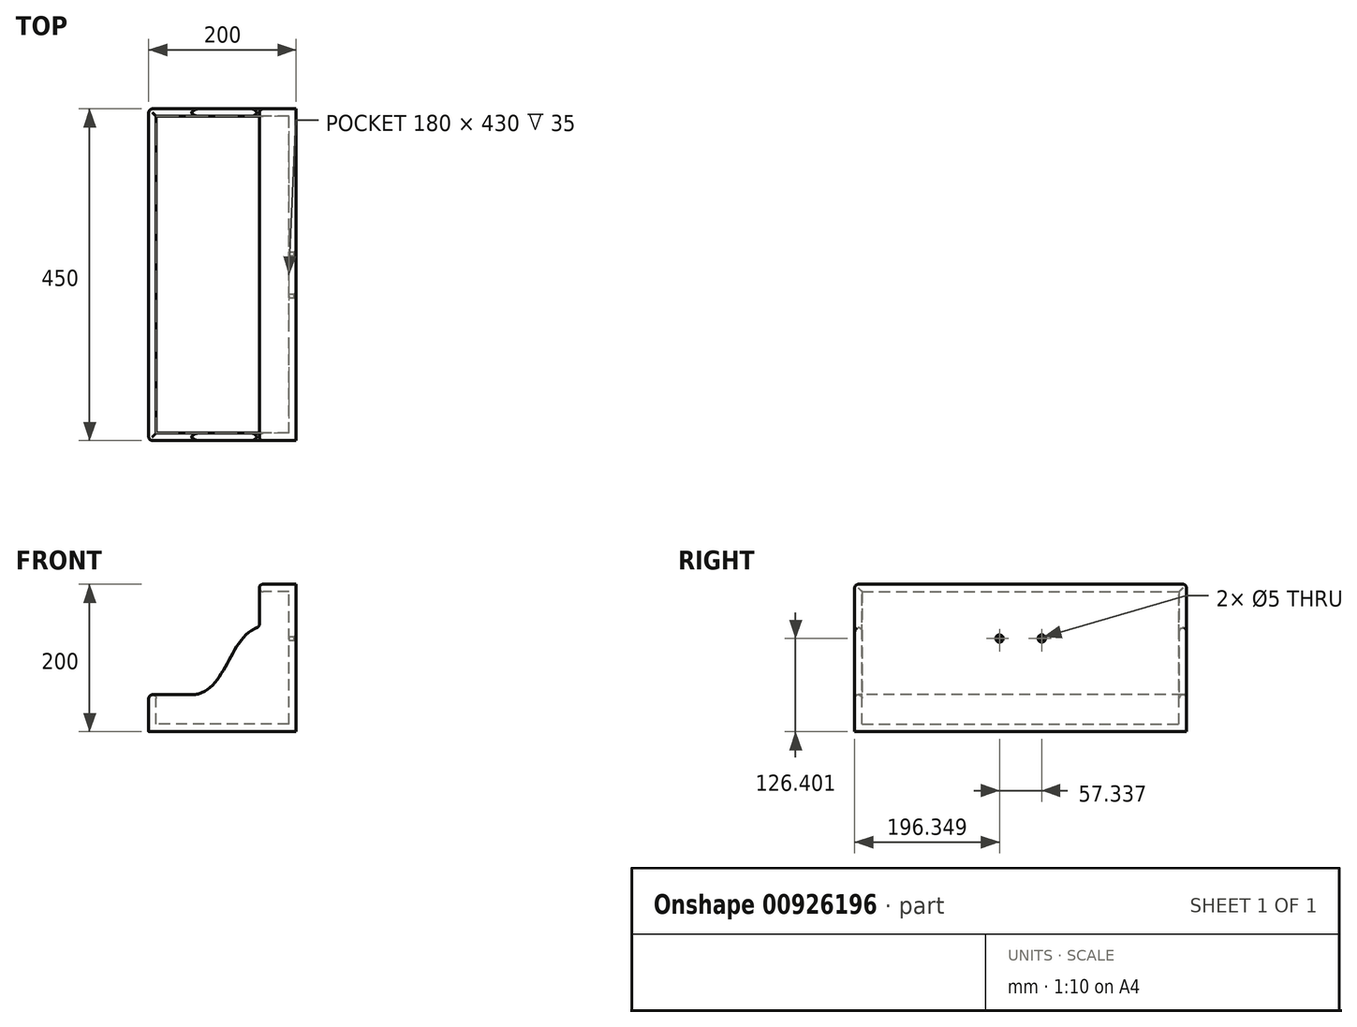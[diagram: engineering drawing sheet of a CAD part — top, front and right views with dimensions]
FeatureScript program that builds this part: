
annotation { "Feature Type Name" : "Feature", "Feature Type Description" : "" }
export const myFeature = defineFeature(function(context is Context, id is Id, definition is map)
    precondition{}
    {
        {
            var Q0;
            Q0=qCreatedBy(makeId("Front.planeOp"),FACE);
            var sketch = newSketch(context, id + "F0", { "sketchPlane" : qUnion([Q0])});
            skLineSegment(sketch, "E0", {"start": v(0, 0) * mm, "end": v(-200, 0) * mm});
            skLineSegment(sketch, "E1", {"start": v(-200, 0) * mm, "end": v(-200, 50) * mm});
            skLineSegment(sketch, "E2", {"start": v(-200, 50) * mm, "end": v(-142.3, 50) * mm});
            skLineSegment(sketch, "E3", {"start": v(0, 0) * mm, "end": v(0, 200) * mm});
            skLineSegment(sketch, "E4", {"start": v(0, 200) * mm, "end": v(-50, 200) * mm});
            skLineSegment(sketch, "E5", {"start": v(-50, 200) * mm, "end": v(-50, 142.3) * mm});
            skFitSpline(sketch, "E6", {"points": [v(-142.3, 50) * mm, v(-50, 142.3) * mm], "startDerivative": vector(145.52, 2.79) * mm, "endDerivative": vector(131.39, 42.95) * mm});
            skSolve(sketch);
        }
        {
            var Q0;
            Q0=makeQuery(id+"F0.imprint","IMPRINT",FACE,{"disambiguationData":[TD([[makeQuery(id+"F0.imprint","IMPRINT",EDGE,{"derivedFrom":sQuery(id+"F0.wireOp",EDGE,"E0")}),-1.0]])]});
            extrude(context, id + "F1", {"entities" : qUnion([Q0]), "depth" : 450 * mm, "offsetDistance" : 25 * mm});
        }
        {
            var Q0;
            Q0=makeQuery(id+"F1.opExtrude","SWEPT_FACE",FACE,{"disambiguationData":[OSD([sQuery(id+"F0.wireOp",EDGE,"E6")])]});
            var Q1;
            Q1=makeQuery(id+"F1.opExtrude","SWEPT_FACE",FACE,{"disambiguationData":[OSD([sQuery(id+"F0.wireOp",EDGE,"E5")])]});
            var Q2;
            Q2=makeQuery(id+"F1.opExtrude","SWEPT_FACE",FACE,{"disambiguationData":[OSD([sQuery(id+"F0.wireOp",EDGE,"E2")])]});
            shell(context, id + "F2", {"entities" : qUnion([Q0, Q1, Q2]), "thickness" : 10 * mm});
        }
        {
            var Q0;
            Q0=makeQuery(id+"F1.opExtrude","SWEPT_FACE",FACE,{"disambiguationData":[OSD([sQuery(id+"F0.wireOp",EDGE,"E5")])]});
            var Q1;
            Q1=makeQuery(id+"F1.opExtrude","SWEPT_FACE",FACE,{"disambiguationData":[OSD([sQuery(id+"F0.wireOp",EDGE,"E2")])]});
            var Q2;
            Q2=makeQuery(id+"F1.opExtrude","CAP_EDGE",EDGE,{"disambiguationData":[OSD([sQuery(id+"F0.wireOp",EDGE,"E1")])],"isStart":false});
            var Q3;
            Q3=makeQuery(id+"F1.opExtrude","CAP_EDGE",EDGE,{"disambiguationData":[OSD([sQuery(id+"F0.wireOp",EDGE,"E1")])],"isStart":true});
            var Q4;
            Q4=makeQuery(id+"F1.opExtrude","CAP_EDGE",EDGE,{"disambiguationData":[OSD([sQuery(id+"F0.wireOp",EDGE,"E4")])],"isStart":false});
            var Q5;
            Q5=makeQuery(id+"F1.opExtrude","CAP_EDGE",EDGE,{"disambiguationData":[OSD([sQuery(id+"F0.wireOp",EDGE,"E4")])],"isStart":true});
            fillet(context, id + "F3", {"entities" : qUnion([Q0, Q1, Q2, Q3, Q4, Q5]), "radius" : 5 * mm, "tangentPropagation" : true, "allowEdgeOverflow" : false});
        }
        {
            var Q0;
            Q0=qCreatedBy(makeId("Right.planeOp"),FACE);
            var sketch = newSketch(context, id + "F4", { "sketchPlane" : qUnion([Q0])});
            skLineSegment(sketch, "E7", {"start": v(0, 0) * mm, "end": v(0, 195.47) * mm, "construction": true});
            skLineSegment(sketch, "E8", {"start": v(0, 195.47) * mm, "end": v(-5.23, 200.01) * mm, "construction": true});
            skLineSegment(sketch, "E9", {"start": v(-5.23, 200.01) * mm, "end": v(-444.97, 200.01) * mm, "construction": true});
            skLineSegment(sketch, "E10", {"start": v(-444.97, 200.01) * mm, "end": v(-449.96, 195.47) * mm, "construction": true});
            skLineSegment(sketch, "E11", {"start": v(-449.96, 195.47) * mm, "end": v(-449.96, 0) * mm, "construction": true});
            skLineSegment(sketch, "E12", {"start": v(-449.96, 0) * mm, "end": v(0, 0) * mm, "construction": true});
            skLineSegment(sketch, "E13", {"start": v(-449.96, 97.73) * mm, "end": v(0, 97.73) * mm, "construction": true});
            skLineSegment(sketch, "E14", {"start": v(-224.98, 97.73) * mm, "end": v(-224.98, 200.01) * mm, "construction": true});
            skLineSegment(sketch, "E15", {"start": v(-224.98, 97.73) * mm, "end": v(-196.31, 126.4) * mm, "construction": true});
            skLineSegment(sketch, "E16.MirrorCS", {"start": v(-224.98, 97.73) * mm, "end": v(-253.65, 126.4) * mm, "construction": true});
            skSolve(sketch);
        }
        {
            var Q0;
            Q0=sQuery(id+"F4.wireOp",VERTEX,"E16.MirrorCS.end");
            var Q1;
            Q1=sQuery(id+"F4.wireOp",VERTEX,"E15.end");
            var Q2;
            Q2=makeQuery(id+"F1.opExtrude","SWEPT_BODY",BODY,{"disambiguationData":[OSD([sQuery(id+"F0.wireOp",EDGE,"E0"),sQuery(id+"F0.wireOp",EDGE,"E1"),sQuery(id+"F0.wireOp",EDGE,"E2"),sQuery(id+"F0.wireOp",EDGE,"E3"),sQuery(id+"F0.wireOp",EDGE,"E4"),sQuery(id+"F0.wireOp",EDGE,"E5"),sQuery(id+"F0.wireOp",EDGE,"E6")])]});
            hole(context, id + "F5", {"style" : HoleStyle.C_SINK, "endStyle" : HoleEndStyle.THROUGH, "holeDiameter" : 5 * mm, "cSinkDiameter" : 10 * mm, "cSinkAngle" : 90 * degree, "majorDiameter" : 5 * mm, "isTappedThrough" : true, "tappedDepth" : 12 * mm, "tapClearance" : 3, "locations" : qUnion([Q0, Q1]), "scope" : qUnion([Q2])});
        }
    });
